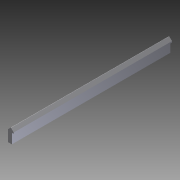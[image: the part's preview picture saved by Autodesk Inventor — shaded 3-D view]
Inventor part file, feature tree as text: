
AUTODESK INVENTOR PART (.ipt)
format: ipt  version: 2014 (Build 180170000, 170)  size: 95,232 bytes
history: native  units: in
note: dims shown in document units (in); Inventor stores cm internally (conversion verified against a paired STEP export)
features: fillet x1, other x1, imported_body x1
ambient origin geometry x8: Origin, YZ Plane, XZ Plane, XY Plane, X Axis, Y Axis, Z Axis, Center Point
bodies: Body1 (feature_tree)
feature tree (3):
  fillet  "Fillet1"  [1 undecoded]
  other  "BWC-T4-11"
  imported_body  "Base1"
note: 1 required parameter value undecoded (feature->parameter linkage not recoverable at this tier; creation-order binding heuristic only, values carry confidence <= 0.55)
